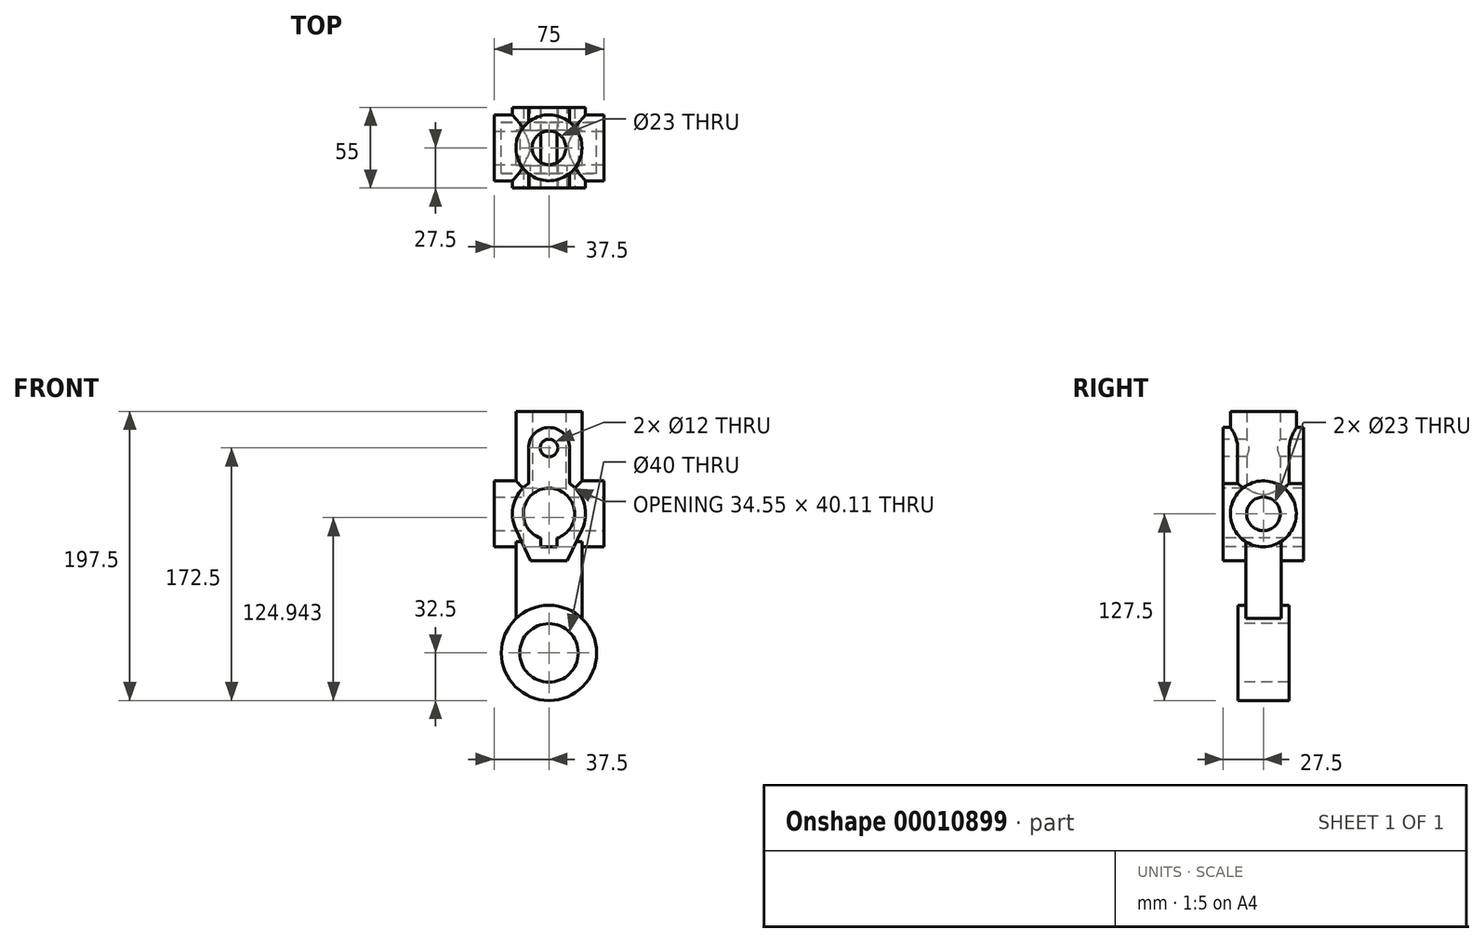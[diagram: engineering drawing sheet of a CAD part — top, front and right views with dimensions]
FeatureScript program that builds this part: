
annotation { "Feature Type Name" : "Feature", "Feature Type Description" : "" }
export const myFeature = defineFeature(function(context is Context, id is Id, definition is map)
    precondition{}
    {
        {
            var Q0;
            Q0=qCreatedBy(makeId("Front.planeOp"),FACE);
            var sketch = newSketch(context, id + "F0", { "sketchPlane" : qUnion([Q0])});
            skLineSegment(sketch, "E0", {"start": v(0, 0) * mm, "end": v(22.5, 0) * mm});
            skLineSegment(sketch, "E1", {"start": v(22.5, 0) * mm, "end": v(22.5, -95) * mm});
            skLineSegment(sketch, "E2", {"start": v(22.5, -95) * mm, "end": v(0, -95) * mm});
            skLineSegment(sketch, "E3", {"start": v(0, 131.5) * mm, "end": v(0, -114.56) * mm, "construction": true});
            skLineSegment(sketch, "E4.0.MirrorCS", {"start": v(0, 0) * mm, "end": v(-22.5, 0) * mm});
            skLineSegment(sketch, "E5.0.MirrorCS", {"start": v(-22.5, 0) * mm, "end": v(-22.5, -95) * mm});
            skLineSegment(sketch, "E6.0.MirrorCS", {"start": v(-22.5, -95) * mm, "end": v(0, -95) * mm});
            skSolve(sketch);
        }
        {
            var Q0;
            Q0=qCreatedBy(makeId("Front.planeOp"),FACE);
            var sketch = newSketch(context, id + "F1", { "sketchPlane" : qUnion([Q0])});
            skCircle(sketch, "E7", {"center": v(0, -95) * mm, "radius": 32.5 * mm});
            skSolve(sketch);
        }
        {
            var Q0;
            Q0=qCreatedBy(makeId("Front.planeOp"),FACE);
            var sketch = newSketch(context, id + "F2", { "sketchPlane" : qUnion([Q0])});
            skLineSegment(sketch, "E8.rect.top", {"start": v(12.5, -32) * mm, "end": v(-12.5, -32) * mm});
            skPoint(sketch, "E8.rect.middle", {"position": v(0, 0) * mm});
            skArc(sketch, "E9", {"start": v(-14, 20.71) * mm, "mid": v(-24.11, 6.6) * mm, "end": v(-22.6, -10.7) * mm});
            skArc(sketch, "E10", {"start": v(14, 45) * mm, "mid": v(0, 59) * mm, "end": v(-14, 45) * mm});
            skLineSegment(sketch, "E11", {"start": v(12.5, -32) * mm, "end": v(22.6, -10.7) * mm});
            skLineSegment(sketch, "E12", {"start": v(-12.5, -32) * mm, "end": v(-22.6, -10.7) * mm});
            skLineSegment(sketch, "E13.rect.left", {"start": v(14, 45) * mm, "end": v(14, 20.71) * mm});
            skLineSegment(sketch, "E13.rect.right", {"start": v(-14, 45) * mm, "end": v(-14, 20.71) * mm});
            skArc(sketch, "E14.trimOffspring", {"start": v(22.6, -10.7) * mm, "mid": v(24.11, 6.6) * mm, "end": v(14, 20.71) * mm});
            skSolve(sketch);
        }
        {
            var Q0;
            Q0=qCreatedBy(makeId("Right.planeOp"),FACE);
            var sketch = newSketch(context, id + "F3", { "sketchPlane" : qUnion([Q0])});
            skCircle(sketch, "E15", {"center": v(0, 0) * mm, "radius": 22.5 * mm});
            skSolve(sketch);
        }
        {
            var Q0;
            Q0=qCreatedBy(makeId("Top.planeOp"),FACE);
            var sketch = newSketch(context, id + "F4", { "sketchPlane" : qUnion([Q0])});
            skCircle(sketch, "E16", {"center": v(0, 0) * mm, "radius": 22.5 * mm});
            skSolve(sketch);
        }
        {
            var Q0;
            Q0 = qSketchRegion(id + "F0", true);
            extrude(context, id + "F5", {"entities" : qUnion([Q0]), "endBound" : BoundingType.SYMMETRIC, "depth" : 24 * mm});
        }
        {
            var Q0;
            Q0 = qSketchRegion(id + "F1", true);
            extrude(context, id + "F6", {"entities" : qUnion([Q0]), "operationType" : NewBodyOperationType.ADD, "endBound" : BoundingType.SYMMETRIC, "depth" : 35 * mm});
        }
        {
            var Q0;
            Q0 = qSketchRegion(id + "F2", true);
            extrude(context, id + "F7", {"entities" : qUnion([Q0]), "operationType" : NewBodyOperationType.ADD, "endBound" : BoundingType.SYMMETRIC, "depth" : 55 * mm});
        }
        {
            var Q0;
            Q0 = qSketchRegion(id + "F3", true);
            extrude(context, id + "F8", {"entities" : qUnion([Q0]), "operationType" : NewBodyOperationType.ADD, "endBound" : BoundingType.SYMMETRIC, "depth" : 75 * mm});
        }
        {
            var Q0;
            Q0 = qSketchRegion(id + "F4", true);
            extrude(context, id + "F9", {"entities" : qUnion([Q0]), "operationType" : NewBodyOperationType.ADD, "depth" : 70 * mm});
        }
        {
            var Q0;
            Q0=makeQuery(id+"F7.opExtrude","CAP_FACE",FACE,{"disambiguationData":[OSD([sQuery(id+"F2.wireOp",EDGE,"E8.rect.top"),sQuery(id+"F2.wireOp",EDGE,"E9"),sQuery(id+"F2.wireOp",EDGE,"E10"),sQuery(id+"F2.wireOp",EDGE,"E11"),sQuery(id+"F2.wireOp",EDGE,"E12"),sQuery(id+"F2.wireOp",EDGE,"E13.rect.left"),sQuery(id+"F2.wireOp",EDGE,"E13.rect.right"),sQuery(id+"F2.wireOp",EDGE,"E14.trimOffspring")])],"isStart":false});
            var sketch = newSketch(context, id + "F10", { "sketchPlane" : qUnion([Q0])});
            skPoint(sketch, "E17.rect.middle", {"position": v(0, 0) * mm});
            skArc(sketch, "E18", {"start": v(5.5, -16.61) * mm, "mid": v(0, 17.5) * mm, "end": v(-5.5, -16.61) * mm});
            skLineSegment(sketch, "E19.top", {"start": v(-5.5, -22.61) * mm, "end": v(5.5, -22.61) * mm});
            skLineSegment(sketch, "E19.left", {"start": v(-5.5, -16.61) * mm, "end": v(-5.5, -22.61) * mm});
            skLineSegment(sketch, "E20.trimOffspring", {"start": v(5.5, -16.61) * mm, "end": v(5.5, -22.61) * mm});
            skCircle(sketch, "E21", {"center": v(0, 45) * mm, "radius": 6 * mm});
            skSolve(sketch);
        }
        {
            var Q0;
            Q0 = qSketchRegion(id + "F10", true);
            extrude(context, id + "F11", {"entities" : qUnion([Q0]), "operationType" : NewBodyOperationType.REMOVE, "endBound" : BoundingType.THROUGH_ALL, "oppositeDirection" : true, "depth" : 25 * mm});
        }
        {
            var Q0;
            Q0=qCreatedBy(makeId("Top.planeOp"),FACE);
            var sketch = newSketch(context, id + "F12", { "sketchPlane" : qUnion([Q0])});
            skCircle(sketch, "E22", {"center": v(0, 0) * mm, "radius": 11.5 * mm});
            skSolve(sketch);
        }
        {
            var Q0;
            Q0 = qSketchRegion(id + "F12", true);
            extrude(context, id + "F13", {"entities" : qUnion([Q0]), "operationType" : NewBodyOperationType.REMOVE, "endBound" : BoundingType.THROUGH_ALL, "depth" : 25 * mm});
        }
        {
            var Q0;
            Q0=makeQuery(id+"F6.opExtrude","CAP_FACE",FACE,{"disambiguationData":[OSD([sQuery(id+"F1.wireOp",EDGE,"E7")])],"isStart":false});
            var sketch = newSketch(context, id + "F14", { "sketchPlane" : qUnion([Q0])});
            skCircle(sketch, "E23", {"center": v(0, -95) * mm, "radius": 20 * mm});
            skSolve(sketch);
        }
        {
            var Q0;
            Q0 = qSketchRegion(id + "F14", true);
            extrude(context, id + "F15", {"entities" : qUnion([Q0]), "operationType" : NewBodyOperationType.REMOVE, "endBound" : BoundingType.THROUGH_ALL, "oppositeDirection" : true, "depth" : 25 * mm});
        }
        {
            var Q0;
            Q0=makeQuery(id+"F8.opExtrude","CAP_FACE",FACE,{"disambiguationData":[OSD([sQuery(id+"F3.wireOp",EDGE,"E15")])],"isStart":false});
            var sketch = newSketch(context, id + "F16", { "sketchPlane" : qUnion([Q0])});
            skCircle(sketch, "E24", {"center": v(0, 0) * mm, "radius": 11.5 * mm});
            skSolve(sketch);
        }
        {
            var Q0;
            Q0 = qSketchRegion(id + "F16", true);
            extrude(context, id + "F17", {"entities" : qUnion([Q0]), "operationType" : NewBodyOperationType.REMOVE, "endBound" : BoundingType.THROUGH_ALL, "oppositeDirection" : true, "depth" : 25 * mm});
        }
    });
